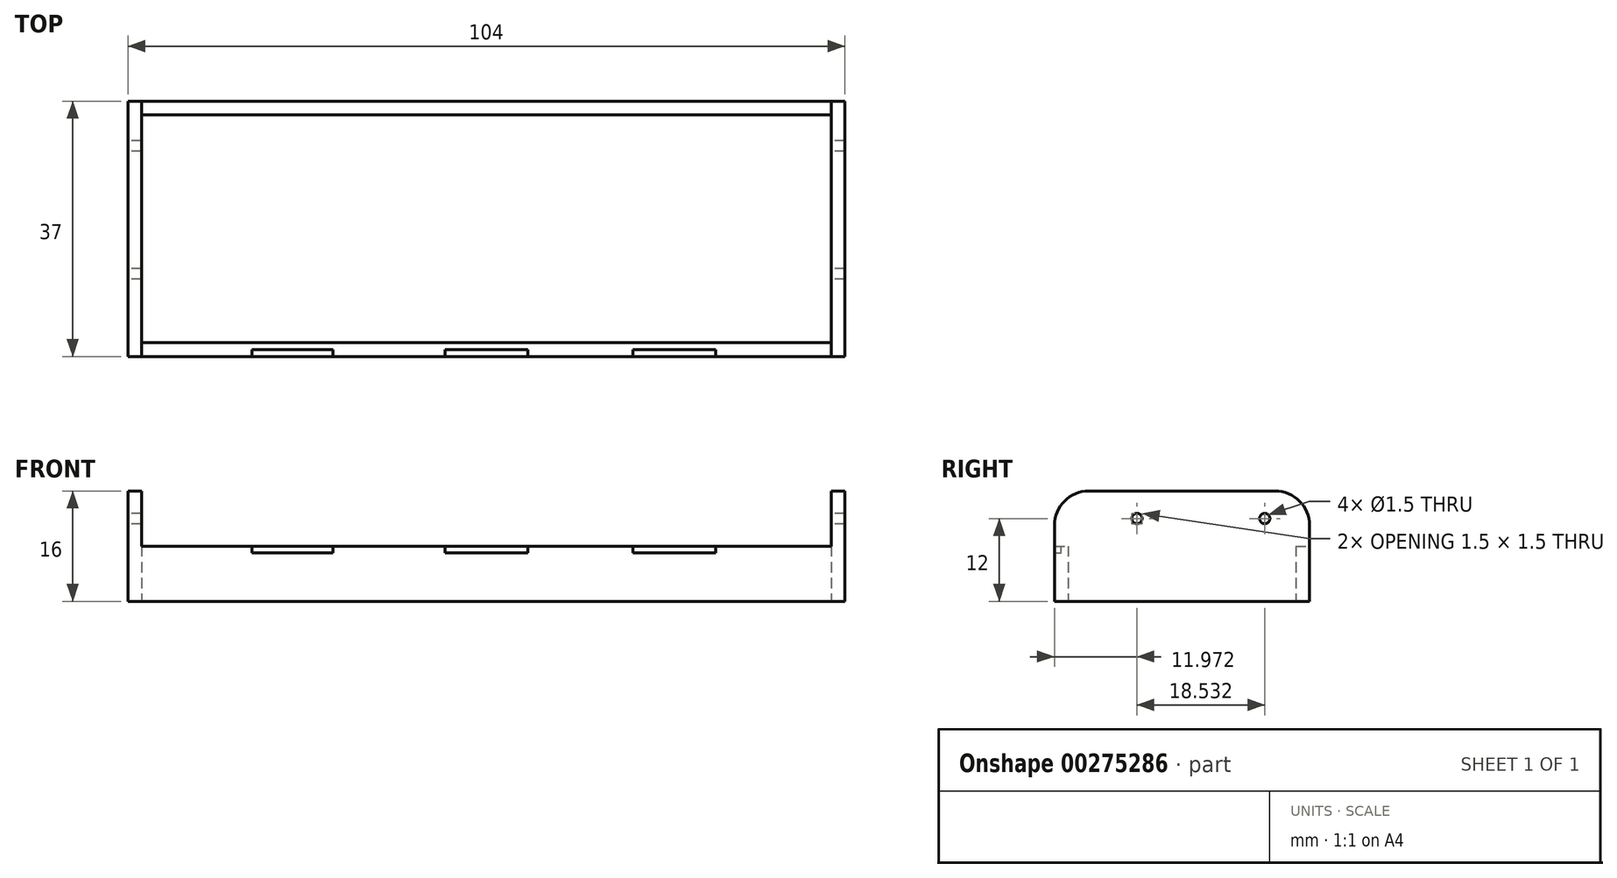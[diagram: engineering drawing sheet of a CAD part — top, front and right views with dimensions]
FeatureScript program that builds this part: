
annotation { "Feature Type Name" : "Feature", "Feature Type Description" : "" }
export const myFeature = defineFeature(function(context is Context, id is Id, definition is map)
    precondition{}
    {
        {
            var Q0;
            Q0=qCreatedBy(makeId("Top.planeOp"),FACE);
            var sketch = newSketch(context, id + "F0", { "sketchPlane" : qUnion([Q0])});
            skLineSegment(sketch, "E0.bottom", {"start": v(0, 0) * mm, "end": v(104, 0) * mm});
            skLineSegment(sketch, "E0.top", {"start": v(0, 37) * mm, "end": v(104, 37) * mm});
            skLineSegment(sketch, "E0.left", {"start": v(0, 0) * mm, "end": v(0, 37) * mm});
            skLineSegment(sketch, "E0.right", {"start": v(104, 0) * mm, "end": v(104, 37) * mm});
            skLineSegment(sketch, "E1.bottom", {"start": v(2, 35) * mm, "end": v(102, 35) * mm});
            skLineSegment(sketch, "E1.top", {"start": v(2, 2) * mm, "end": v(102, 2) * mm});
            skLineSegment(sketch, "E1.left", {"start": v(2, 35) * mm, "end": v(2, 2) * mm});
            skLineSegment(sketch, "E1.right", {"start": v(102, 35) * mm, "end": v(102, 2) * mm});
            skSolve(sketch);
        }
        {
            var Q0;
            Q0=makeQuery(id+"F0.imprint","IMPRINT",FACE,{"disambiguationData":[TD([[makeQuery(id+"F0.imprint","IMPRINT",EDGE,{"derivedFrom":sQuery(id+"F0.wireOp",EDGE,"E0.bottom")}),1.0]])]});
            extrude(context, id + "F1", {"entities" : qUnion([Q0]), "depth" : 8 * mm});
        }
        {
            var Q0;
            Q0=makeQuery(id+"F1.opExtrude","CAP_FACE",FACE,{"disambiguationData":[OSD([sQuery(id+"F0.wireOp",EDGE,"E0.bottom"),sQuery(id+"F0.wireOp",EDGE,"E0.top"),sQuery(id+"F0.wireOp",EDGE,"E0.left"),sQuery(id+"F0.wireOp",EDGE,"E0.right"),sQuery(id+"F0.wireOp",EDGE,"E1.bottom"),sQuery(id+"F0.wireOp",EDGE,"E1.top"),sQuery(id+"F0.wireOp",EDGE,"E1.left"),sQuery(id+"F0.wireOp",EDGE,"E1.right")])],"isStart":false});
            var sketch = newSketch(context, id + "F2", { "sketchPlane" : qUnion([Q0])});
            skLineSegment(sketch, "E2.0", {"start": v(2, 0) * mm, "end": v(46, 0) * mm, "construction": true});
            skLineSegment(sketch, "E3.bottom", {"start": v(52, 0) * mm, "end": v(58, 0) * mm});
            skLineSegment(sketch, "E3.top", {"start": v(52, 1) * mm, "end": v(58, 1) * mm});
            skLineSegment(sketch, "E3.left", {"start": v(52, 0) * mm, "end": v(52, 1) * mm, "construction": true});
            skLineSegment(sketch, "E3.right", {"start": v(58, 0) * mm, "end": v(58, 1) * mm});
            skLineSegment(sketch, "E4.MirrorCS", {"start": v(46, 0) * mm, "end": v(46, 1) * mm});
            skLineSegment(sketch, "E5.MirrorCS", {"start": v(52, 1) * mm, "end": v(46, 1) * mm});
            skLineSegment(sketch, "E6.MirrorCS", {"start": v(52, 0) * mm, "end": v(46, 0) * mm});
            skPoint(sketch, "E7.orphan", {"position": v(104, 0) * mm});
            skPoint(sketch, "E8", {"position": v(2, 0) * mm});
            skPoint(sketch, "E9.orphan", {"position": v(0, 0) * mm});
            skPoint(sketch, "E10", {"position": v(24, 0) * mm});
            skLineSegment(sketch, "E11.bottom", {"start": v(24, 0) * mm, "end": v(18, 0) * mm});
            skLineSegment(sketch, "E11.top", {"start": v(23.75, 1) * mm, "end": v(18, 1) * mm});
            skLineSegment(sketch, "E11.right", {"start": v(18, 0) * mm, "end": v(18, 1) * mm});
            skLineSegment(sketch, "E12.bottom", {"start": v(24, 0) * mm, "end": v(29.75, 0) * mm});
            skLineSegment(sketch, "E12.top", {"start": v(23.75, 1) * mm, "end": v(29.75, 1) * mm});
            skLineSegment(sketch, "E12.right", {"start": v(29.75, 0) * mm, "end": v(29.75, 1) * mm});
            skPoint(sketch, "E13", {"position": v(102, 0) * mm});
            skLineSegment(sketch, "E14", {"start": v(58, 0) * mm, "end": v(102, 0) * mm, "construction": true});
            skPoint(sketch, "E15", {"position": v(80, 0) * mm});
            skLineSegment(sketch, "E16.bottom", {"start": v(80, 0) * mm, "end": v(73.25, 0) * mm});
            skLineSegment(sketch, "E16.top", {"start": v(79.25, 1) * mm, "end": v(73.25, 1) * mm});
            skLineSegment(sketch, "E16.right", {"start": v(73.25, 0) * mm, "end": v(73.25, 1) * mm});
            skLineSegment(sketch, "E17.bottom", {"start": v(80, 0) * mm, "end": v(85.25, 0) * mm});
            skLineSegment(sketch, "E17.top", {"start": v(79.25, 1) * mm, "end": v(85.25, 1) * mm});
            skLineSegment(sketch, "E17.right", {"start": v(85.25, 0) * mm, "end": v(85.25, 1) * mm});
            skSolve(sketch);
        }
        {
            var Q0;
            Q0=qSketchRegion(id+"F2",true);
            extrude(context, id + "F3", {"entities" : qUnion([Q0]), "operationType" : NewBodyOperationType.REMOVE, "oppositeDirection" : true, "depth" : 1 * mm});
        }
        {
            var Q0;
            Q0=makeQuery(id+"F1.opExtrude","CAP_FACE",FACE,{"disambiguationData":[OSD([sQuery(id+"F0.wireOp",EDGE,"E0.bottom"),sQuery(id+"F0.wireOp",EDGE,"E0.top"),sQuery(id+"F0.wireOp",EDGE,"E0.left"),sQuery(id+"F0.wireOp",EDGE,"E0.right"),sQuery(id+"F0.wireOp",EDGE,"E1.bottom"),sQuery(id+"F0.wireOp",EDGE,"E1.top"),sQuery(id+"F0.wireOp",EDGE,"E1.left"),sQuery(id+"F0.wireOp",EDGE,"E1.right")])],"isStart":false});
            var sketch = newSketch(context, id + "F4", { "sketchPlane" : qUnion([Q0])});
            skLineSegment(sketch, "E18.0", {"start": v(0, 0) * mm, "end": v(0, 37) * mm});
            skLineSegment(sketch, "E19.0", {"start": v(2, 35) * mm, "end": v(2, 2) * mm});
            skLineSegment(sketch, "E20.0", {"start": v(102, 35) * mm, "end": v(102, 2) * mm});
            skLineSegment(sketch, "E21.0", {"start": v(104, 0) * mm, "end": v(104, 37) * mm});
            skPoint(sketch, "E22", {"position": v(2, 37) * mm});
            skLineSegment(sketch, "E23", {"start": v(0, 37) * mm, "end": v(2, 37) * mm});
            skLineSegment(sketch, "E24", {"start": v(2, 37) * mm, "end": v(2, 35) * mm});
            skLineSegment(sketch, "E25", {"start": v(102, 35) * mm, "end": v(102, 37) * mm});
            skLineSegment(sketch, "E26", {"start": v(0, 0) * mm, "end": v(2, 0) * mm});
            skLineSegment(sketch, "E27", {"start": v(2, 0) * mm, "end": v(2, 2) * mm});
            skLineSegment(sketch, "E28", {"start": v(102, 2) * mm, "end": v(102, 0) * mm});
            skLineSegment(sketch, "E29", {"start": v(102, 0) * mm, "end": v(104, 0) * mm});
            skSolve(sketch);
        }
        {
            var Q0;
            Q0=makeQuery(id+"F4.imprint","IMPRINT",FACE,{"disambiguationData":[TD([[makeQuery(id+"F4.imprint","IMPRINT",EDGE,{"derivedFrom":sQuery(id+"F4.wireOp",EDGE,"E18.0")}),-1.0]])]});
            var Q1;
            Q1=makeQuery(id+"F4.imprint","IMPRINT",FACE,{"disambiguationData":[TD([[makeQuery(id+"F4.imprint","IMPRINT",EDGE,{"derivedFrom":sQuery(id+"F4.wireOp",EDGE,"E20.0")}),1.0]])]});
            extrude(context, id + "F5", {"entities" : qUnion([Q0, Q1]), "operationType" : NewBodyOperationType.ADD, "depth" : 8 * mm});
        }
        {
            var Q0;
            Q0=makeQuery(id+"F5.boolean.opBoolean","MERGE",FACE,{"derivedFrom":[makeQuery(id+"F1.opExtrude","SWEPT_FACE",FACE,{"disambiguationData":[OSD([sQuery(id+"F0.wireOp",EDGE,"E1.right")])]}),makeQuery(id+"F5.opExtrude","SWEPT_FACE",FACE,{"disambiguationData":[OSD([sQuery(id+"F4.wireOp",EDGE,"E20.0"),sQuery(id+"F4.wireOp",EDGE,"E25"),sQuery(id+"F4.wireOp",EDGE,"E28")])]})]});
            var sketch = newSketch(context, id + "F6", { "sketchPlane" : qUnion([Q0])});
            skPoint(sketch, "E30.0", {"position": v(-37, 12) * mm});
            skPoint(sketch, "E31.0", {"position": v(0, 12) * mm});
            skLineSegment(sketch, "E32", {"start": v(-37, 12) * mm, "end": v(0, 12) * mm, "construction": true});
            skPoint(sketch, "E33", {"position": v(-30.5, 12) * mm});
            skPoint(sketch, "E34", {"position": v(-11.97, 12) * mm});
            skCircle(sketch, "E35", {"center": v(-30.5, 12) * mm, "radius": 0.75 * mm});
            skCircle(sketch, "E36", {"center": v(-11.97, 12) * mm, "radius": 0.75 * mm});
            skLineSegment(sketch, "E37", {"start": v(-37, 8) * mm, "end": v(-37, 11) * mm});
            skLineSegment(sketch, "E38.bottom", {"start": v(-37, 11) * mm, "end": v(-35, 11) * mm});
            skLineSegment(sketch, "E38.top", {"start": v(-37, 16) * mm, "end": v(-35, 16) * mm});
            skLineSegment(sketch, "E38.left", {"start": v(-37, 11) * mm, "end": v(-37, 16) * mm});
            skLineSegment(sketch, "E38.right", {"start": v(-35, 11) * mm, "end": v(-35, 16) * mm});
            skSolve(sketch);
        }
        {
            var Q0;
            Q0=makeQuery(id+"F6.imprint","IMPRINT",FACE,{"disambiguationData":[TD([[makeQuery(id+"F6.imprint","IMPRINT",EDGE,{"derivedFrom":sQuery(id+"F6.wireOp",EDGE,"E35")}),1.0]])]});
            var Q1;
            Q1=makeQuery(id+"F6.imprint","IMPRINT",FACE,{"disambiguationData":[TD([[makeQuery(id+"F6.imprint","IMPRINT",EDGE,{"derivedFrom":sQuery(id+"F6.wireOp",EDGE,"E36")}),1.0]])]});
            extrude(context, id + "F7", {"entities" : qUnion([Q0, Q1]), "operationType" : NewBodyOperationType.REMOVE, "oppositeDirection" : true, "depth" : 10.7 * mm, "hasSecondDirection" : true, "secondDirectionOppositeDirection" : false, "secondDirectionDepth" : 110.5 * mm});
        }
        {
            var Q0;
            Q0=makeQuery(id+"F5.opExtrude","CAP_EDGE",EDGE,{"disambiguationData":[OSD([sQuery(id+"F4.wireOp",EDGE,"E26")])],"isStart":false});
            var Q1;
            Q1=makeQuery(id+"F5.opExtrude","CAP_EDGE",EDGE,{"disambiguationData":[OSD([sQuery(id+"F4.wireOp",EDGE,"E29")])],"isStart":false});
            var Q2;
            Q2=makeQuery(id+"FQpRelEbPUrjk0O_1.boolean.opBoolean","MERGE",EDGE,{"derivedFrom":[makeQuery(id+"F5.opExtrude","CAP_EDGE",EDGE,{"disambiguationData":[OSD([sQuery(id+"F4.wireOp",EDGE,"E23")])],"isStart":false}),makeQuery(id+"F5.opExtrude","CAP_EDGE",EDGE,{"disambiguationData":[OSD([sQuery(id+"F0.wireOp",EDGE,"E0.top")])],"isStart":false}),makeQuery(id+"FQpRelEbPUrjk0O_1.opExtrude","SWEPT_EDGE",EDGE,{"disambiguationData":[OSD([sQuery(id+"F6.wireOp",EDGE,"E38.top"),sQuery(id+"F6.wireOp",EDGE,"E38.left")])]})]});
            fillet(context, id + "F8", {"entities" : qUnion([Q0, Q1, Q2]), "radius" : 5 * mm, "tangentPropagation" : true, "allowEdgeOverflow" : false});
        }
    });
